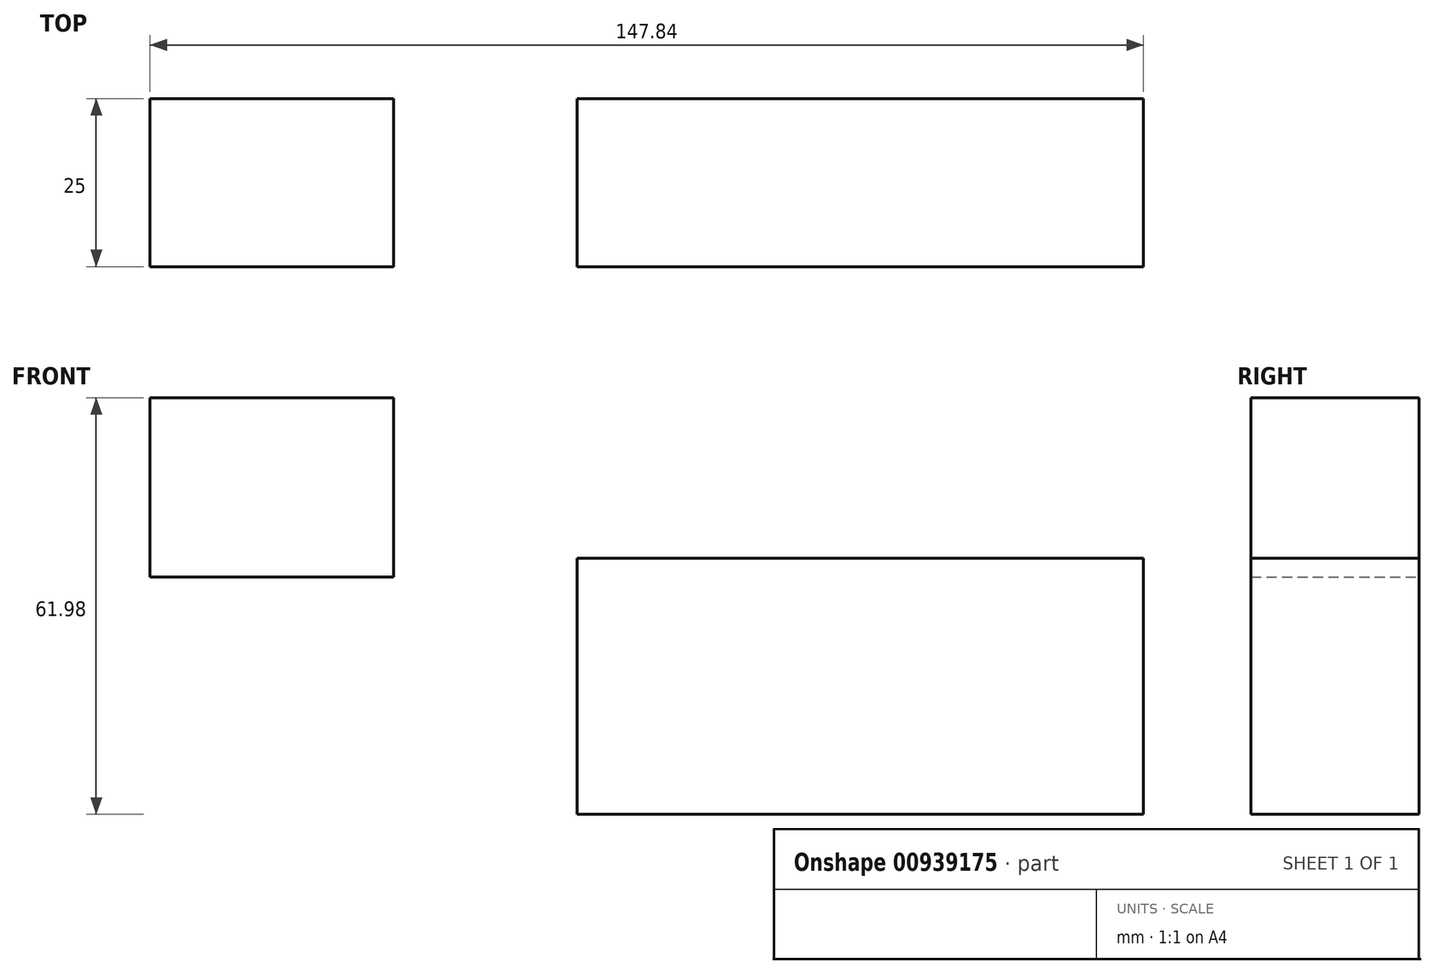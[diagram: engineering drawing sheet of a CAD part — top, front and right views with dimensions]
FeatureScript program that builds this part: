
annotation { "Feature Type Name" : "Feature", "Feature Type Description" : "" }
export const myFeature = defineFeature(function(context is Context, id is Id, definition is map)
    precondition{}
    {
        {
            var Q0;
            Q0=qCreatedBy(makeId("Front.planeOp"),FACE);
            var sketch = newSketch(context, id + "F0", { "sketchPlane" : qUnion([Q0])});
            skLineSegment(sketch, "E0.bottom", {"start": v(-163.16, 61.98) * mm, "end": v(-126.9, 61.98) * mm});
            skLineSegment(sketch, "E0.top", {"start": v(-163.16, 35.27) * mm, "end": v(-126.9, 35.27) * mm});
            skLineSegment(sketch, "E0.left", {"start": v(-163.16, 61.98) * mm, "end": v(-163.16, 35.27) * mm});
            skLineSegment(sketch, "E0.right", {"start": v(-126.9, 61.98) * mm, "end": v(-126.9, 35.27) * mm});
            skLineSegment(sketch, "E1.bottom", {"start": v(-99.64, 38.09) * mm, "end": v(-15.32, 38.09) * mm});
            skLineSegment(sketch, "E1.top", {"start": v(-99.64, 0) * mm, "end": v(-15.32, 0) * mm});
            skLineSegment(sketch, "E1.left", {"start": v(-99.64, 38.09) * mm, "end": v(-99.64, 0) * mm});
            skLineSegment(sketch, "E1.right", {"start": v(-15.32, 38.09) * mm, "end": v(-15.32, 0) * mm});
            skSolve(sketch);
        }
        {
            var Q0;
            Q0=makeQuery(id+"F0.imprint","IMPRINT",FACE,{"disambiguationData":[TD([[makeQuery(id+"F0.imprint","IMPRINT",EDGE,{"derivedFrom":sQuery(id+"F0.wireOp",EDGE,"E1.bottom")}),-1.0]])]});
            var Q1;
            Q1=makeQuery(id+"F0.imprint","IMPRINT",FACE,{"disambiguationData":[TD([[makeQuery(id+"F0.imprint","IMPRINT",EDGE,{"derivedFrom":sQuery(id+"F0.wireOp",EDGE,"E0.bottom")}),-1.0]])]});
            extrude(context, id + "F1", {"entities" : qUnion([Q0, Q1]), "depth" : 25 * mm, "offsetDistance" : 25 * mm});
        }
    });
